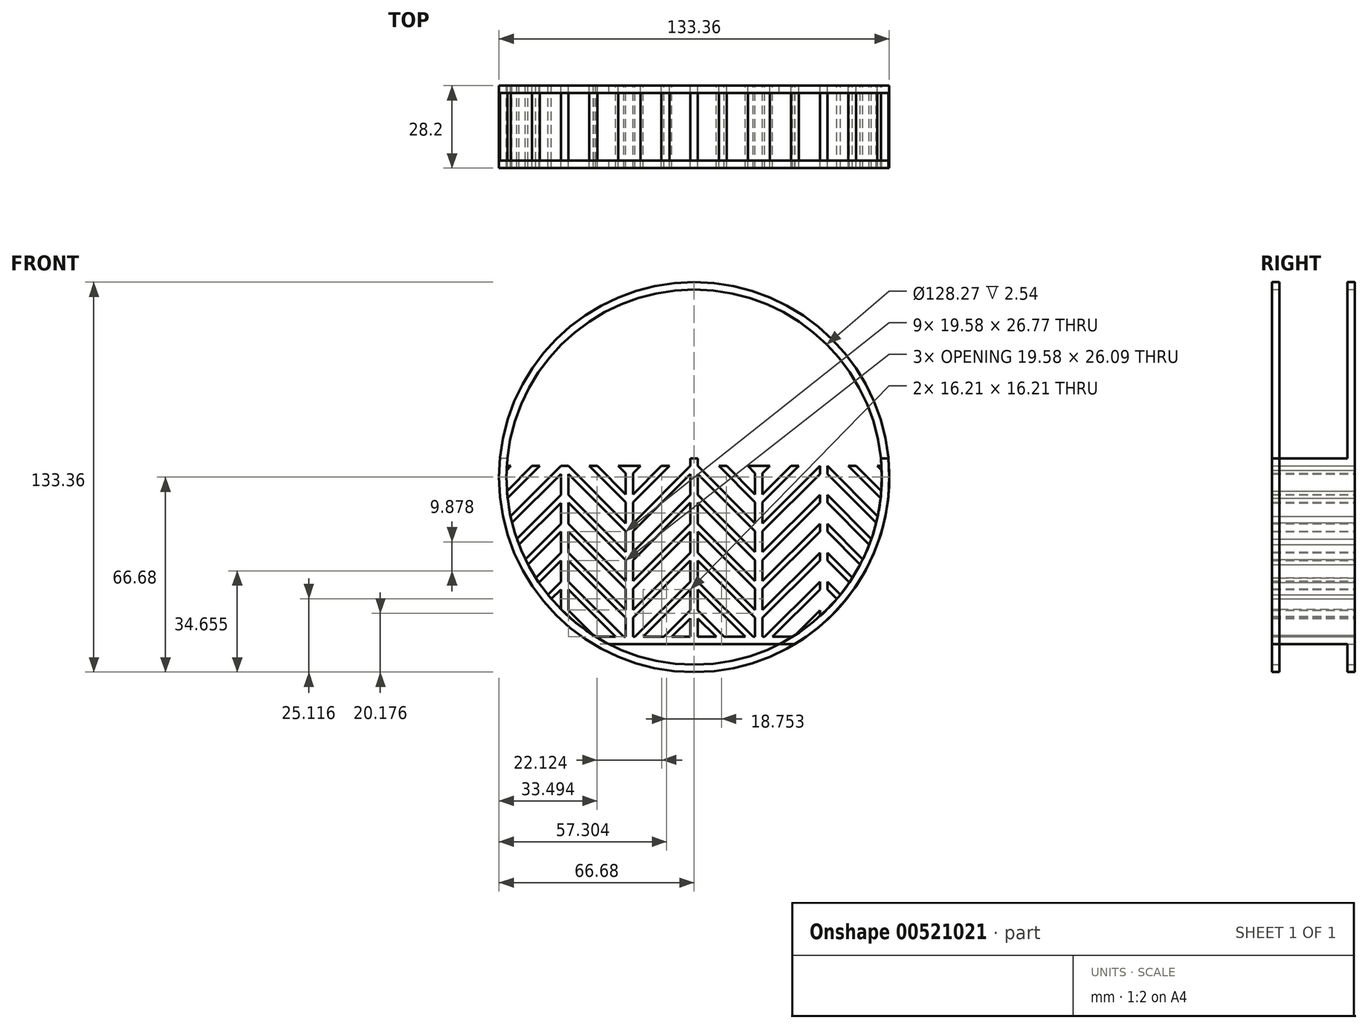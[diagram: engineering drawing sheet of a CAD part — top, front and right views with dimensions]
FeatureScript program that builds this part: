
annotation { "Feature Type Name" : "Feature", "Feature Type Description" : "" }
export const myFeature = defineFeature(function(context is Context, id is Id, definition is map)
    precondition{}
    {
        {
            var Q0;
            Q0=qCreatedBy(makeId("Front.planeOp"),FACE);
            var sketch = newSketch(context, id + "F0", { "sketchPlane" : qUnion([Q0])});
            skCircle(sketch, "E0", {"center": v(0, 0) * mm, "radius": 66.68 * mm, "construction": true});
            skLineSegment(sketch, "E1", {"start": v(-66.37, 6.35) * mm, "end": v(66.37, 6.35) * mm});
            skLineSegment(sketch, "E2", {"start": v(-34.34, -57.15) * mm, "end": v(34.34, -57.15) * mm});
            skArc(sketch, "E3", {"start": v(-66.37, 6.35) * mm, "mid": v(-59.53, -30.03) * mm, "end": v(-34.34, -57.15) * mm});
            skArc(sketch, "E4", {"start": v(66.37, 6.35) * mm, "mid": v(59.53, -30.03) * mm, "end": v(34.34, -57.15) * mm});
            skLineSegment(sketch, "E5", {"start": v(0, 6.35) * mm, "end": v(0, -57.15) * mm});
            skLineSegment(sketch, "E6", {"start": v(0, 6.35) * mm, "end": v(-22.12, 6.35) * mm});
            skLineSegment(sketch, "E7", {"start": v(-22.12, 6.35) * mm, "end": v(-44.25, 6.35) * mm});
            skLineSegment(sketch, "E8", {"start": v(-44.25, 6.35) * mm, "end": v(-66.37, 6.35) * mm});
            skLineSegment(sketch, "E9", {"start": v(0, 6.35) * mm, "end": v(22.12, 6.35) * mm});
            skLineSegment(sketch, "E10", {"start": v(22.12, 6.35) * mm, "end": v(44.25, 6.35) * mm});
            skLineSegment(sketch, "E11", {"start": v(44.25, 6.35) * mm, "end": v(66.37, 6.35) * mm});
            skLineSegment(sketch, "E12", {"start": v(-44.25, 6.35) * mm, "end": v(-44.25, -49.88) * mm, "construction": true});
            skLineSegment(sketch, "E13", {"start": v(-22.12, 6.35) * mm, "end": v(-22.12, -57.15) * mm, "construction": true});
            skLineSegment(sketch, "E14", {"start": v(22.12, 6.35) * mm, "end": v(22.12, -57.15) * mm, "construction": true});
            skLineSegment(sketch, "E15", {"start": v(44.25, 6.35) * mm, "end": v(44.25, -49.88) * mm, "construction": true});
            skCircle(sketch, "E16", {"center": v(0, 0) * mm, "radius": 64.14 * mm, "construction": true});
            skArc(sketch, "E17", {"start": v(-63.82, 6.35) * mm, "mid": v(-56.28, -30.76) * mm, "end": v(-29.1, -57.15) * mm});
            skArc(sketch, "E18", {"start": v(63.82, 6.35) * mm, "mid": v(56.28, -30.76) * mm, "end": v(29.1, -57.15) * mm});
            skLineSegment(sketch, "E19", {"start": v(-45.52, 6.35) * mm, "end": v(-45.52, -45.18) * mm});
            skLineSegment(sketch, "E20", {"start": v(-42.98, 6.35) * mm, "end": v(-42.98, -47.6) * mm});
            skLineSegment(sketch, "E21", {"start": v(-23.4, 6.35) * mm, "end": v(-23.4, -57.15) * mm});
            skLineSegment(sketch, "E22", {"start": v(-20.85, 6.35) * mm, "end": v(-20.85, -57.15) * mm});
            skLineSegment(sketch, "E23", {"start": v(-1.27, 6.35) * mm, "end": v(-1.27, -57.15) * mm});
            skLineSegment(sketch, "E24", {"start": v(1.27, 6.35) * mm, "end": v(1.27, -57.15) * mm});
            skLineSegment(sketch, "E25", {"start": v(20.85, 6.35) * mm, "end": v(20.85, -57.15) * mm});
            skLineSegment(sketch, "E26", {"start": v(23.4, 6.35) * mm, "end": v(23.4, -57.15) * mm});
            skLineSegment(sketch, "E27", {"start": v(42.98, 6.35) * mm, "end": v(42.98, -47.6) * mm});
            skLineSegment(sketch, "E28", {"start": v(45.52, 6.35) * mm, "end": v(45.52, -45.18) * mm});
            skLineSegment(sketch, "E29", {"start": v(-66.57, 3.81) * mm, "end": v(64.02, 3.81) * mm});
            skLineSegment(sketch, "E30", {"start": v(-33.63, -54.61) * mm, "end": v(33.63, -54.61) * mm});
            skLineSegment(sketch, "E31", {"start": v(-63.96, -4.75) * mm, "end": v(-55.4, 3.81) * mm});
            skLineSegment(sketch, "E32", {"start": v(-63.73, -7.22) * mm, "end": v(-52.7, 3.81) * mm});
            skLineSegment(sketch, "E33", {"start": v(-62.72, -13.4) * mm, "end": v(-45.52, 3.81) * mm});
            skLineSegment(sketch, "E34", {"start": v(-62.21, -15.58) * mm, "end": v(-45.52, 1.12) * mm});
            skLineSegment(sketch, "E35", {"start": v(-60.56, -21.11) * mm, "end": v(-45.52, -6.07) * mm});
            skLineSegment(sketch, "E36", {"start": v(-59.83, -23.1) * mm, "end": v(-45.52, -8.8) * mm});
            skLineSegment(sketch, "E37", {"start": v(-57.65, -28.1) * mm, "end": v(-45.52, -15.98) * mm});
            skLineSegment(sketch, "E38", {"start": v(-56.74, -29.9) * mm, "end": v(-45.52, -18.67) * mm});
            skLineSegment(sketch, "E39", {"start": v(-54.1, -34.44) * mm, "end": v(-45.52, -25.85) * mm});
            skLineSegment(sketch, "E40", {"start": v(-53.03, -36.06) * mm, "end": v(-45.52, -28.55) * mm});
            skLineSegment(sketch, "E41", {"start": v(-49.98, -40.2) * mm, "end": v(-45.52, -35.73) * mm});
            skLineSegment(sketch, "E42", {"start": v(-48.76, -41.67) * mm, "end": v(-45.52, -38.43) * mm});
            skLineSegment(sketch, "E43", {"start": v(-64.1, 2.3) * mm, "end": v(-62.58, 3.81) * mm});
            skLineSegment(sketch, "E44", {"start": v(-52.7, 3.81) * mm, "end": v(-52.7, 6.35) * mm, "construction": true});
            skLineSegment(sketch, "E45", {"start": v(-42.98, 3.81) * mm, "end": v(-23.4, -15.77) * mm});
            skLineSegment(sketch, "E46", {"start": v(-42.98, 1.12) * mm, "end": v(-23.4, -18.47) * mm});
            skLineSegment(sketch, "E47", {"start": v(-42.98, -6.07) * mm, "end": v(-23.4, -25.65) * mm});
            skLineSegment(sketch, "E48", {"start": v(-42.98, -8.76) * mm, "end": v(-23.4, -28.35) * mm});
            skLineSegment(sketch, "E49", {"start": v(-42.98, -15.95) * mm, "end": v(-23.4, -35.53) * mm});
            skLineSegment(sketch, "E50", {"start": v(-42.98, -18.64) * mm, "end": v(-23.4, -38.22) * mm});
            skLineSegment(sketch, "E51", {"start": v(-42.98, -25.82) * mm, "end": v(-23.4, -45.4) * mm});
            skLineSegment(sketch, "E52", {"start": v(-42.98, -28.52) * mm, "end": v(-23.4, -48.1) * mm});
            skLineSegment(sketch, "E53", {"start": v(-42.98, -35.7) * mm, "end": v(-24.07, -54.61) * mm});
            skLineSegment(sketch, "E54", {"start": v(-42.98, -45.58) * mm, "end": v(-34.48, -54.08) * mm});
            skLineSegment(sketch, "E55", {"start": v(-42.98, -38.4) * mm, "end": v(-26.77, -54.61) * mm});
            skLineSegment(sketch, "E56", {"start": v(-35.8, 3.81) * mm, "end": v(-23.4, -8.59) * mm});
            skLineSegment(sketch, "E57", {"start": v(-33.1, 3.81) * mm, "end": v(-23.4, -5.9) * mm});
            skLineSegment(sketch, "E58", {"start": v(-25.92, 3.81) * mm, "end": v(-23.4, 1.29) * mm});
            skLineSegment(sketch, "E59", {"start": v(-1.27, 3.81) * mm, "end": v(-20.85, -15.77) * mm});
            skLineSegment(sketch, "E60", {"start": v(-8.45, 3.81) * mm, "end": v(-20.85, -8.59) * mm});
            skLineSegment(sketch, "E61", {"start": v(-11.15, 3.81) * mm, "end": v(-20.85, -5.9) * mm});
            skLineSegment(sketch, "E62", {"start": v(-18.33, 3.81) * mm, "end": v(-20.85, 1.29) * mm});
            skLineSegment(sketch, "E63", {"start": v(-1.27, 1.12) * mm, "end": v(-20.85, -18.47) * mm});
            skLineSegment(sketch, "E64", {"start": v(-20.85, -25.65) * mm, "end": v(-1.27, -6.07) * mm});
            skLineSegment(sketch, "E65", {"start": v(-20.85, -28.35) * mm, "end": v(-1.27, -8.76) * mm});
            skLineSegment(sketch, "E66", {"start": v(-20.85, -35.53) * mm, "end": v(-1.27, -15.95) * mm});
            skLineSegment(sketch, "E67", {"start": v(-20.85, -38.22) * mm, "end": v(-1.27, -18.64) * mm});
            skLineSegment(sketch, "E68", {"start": v(-20.85, -45.4) * mm, "end": v(-1.27, -25.82) * mm});
            skLineSegment(sketch, "E69", {"start": v(-20.85, -48.1) * mm, "end": v(-1.27, -28.52) * mm});
            skLineSegment(sketch, "E70", {"start": v(-20.18, -54.61) * mm, "end": v(-1.27, -35.7) * mm});
            skLineSegment(sketch, "E71", {"start": v(-17.48, -54.61) * mm, "end": v(-1.27, -38.4) * mm});
            skLineSegment(sketch, "E72", {"start": v(-10.3, -54.61) * mm, "end": v(-1.27, -45.58) * mm});
            skLineSegment(sketch, "E73", {"start": v(-7.6, -54.61) * mm, "end": v(-1.27, -48.28) * mm});
            skLineSegment(sketch, "E74", {"start": v(1.27, 3.81) * mm, "end": v(20.85, -15.77) * mm});
            skLineSegment(sketch, "E75", {"start": v(1.27, 1.12) * mm, "end": v(20.85, -18.47) * mm});
            skLineSegment(sketch, "E76", {"start": v(1.27, -6.07) * mm, "end": v(20.85, -25.65) * mm});
            skLineSegment(sketch, "E77", {"start": v(1.27, -8.76) * mm, "end": v(20.85, -28.35) * mm});
            skLineSegment(sketch, "E78", {"start": v(1.27, -15.95) * mm, "end": v(20.85, -35.53) * mm});
            skLineSegment(sketch, "E79", {"start": v(1.27, -18.64) * mm, "end": v(20.85, -38.22) * mm});
            skLineSegment(sketch, "E80", {"start": v(1.27, -25.82) * mm, "end": v(20.85, -45.4) * mm});
            skLineSegment(sketch, "E81", {"start": v(1.27, -28.52) * mm, "end": v(20.85, -48.1) * mm});
            skLineSegment(sketch, "E82", {"start": v(1.27, -35.7) * mm, "end": v(20.18, -54.61) * mm});
            skLineSegment(sketch, "E83", {"start": v(1.27, -38.4) * mm, "end": v(17.48, -54.61) * mm});
            skLineSegment(sketch, "E84", {"start": v(1.27, -45.58) * mm, "end": v(10.3, -54.61) * mm});
            skLineSegment(sketch, "E85", {"start": v(1.27, -48.28) * mm, "end": v(7.6, -54.61) * mm});
            skLineSegment(sketch, "E86", {"start": v(8.45, 3.81) * mm, "end": v(20.85, -8.59) * mm});
            skLineSegment(sketch, "E87", {"start": v(11.15, 3.81) * mm, "end": v(20.85, -5.9) * mm});
            skLineSegment(sketch, "E88", {"start": v(18.33, 3.81) * mm, "end": v(20.85, 1.29) * mm});
            skLineSegment(sketch, "E89", {"start": v(23.4, -5.9) * mm, "end": v(33.1, 3.81) * mm});
            skLineSegment(sketch, "E90", {"start": v(23.4, 1.29) * mm, "end": v(25.92, 3.81) * mm});
            skLineSegment(sketch, "E91", {"start": v(23.4, -15.77) * mm, "end": v(42.98, 3.81) * mm});
            skLineSegment(sketch, "E92", {"start": v(23.4, -8.59) * mm, "end": v(35.8, 3.81) * mm});
            skLineSegment(sketch, "E93", {"start": v(23.4, -18.47) * mm, "end": v(42.98, 1.12) * mm});
            skLineSegment(sketch, "E94", {"start": v(23.4, -25.65) * mm, "end": v(42.98, -6.07) * mm});
            skLineSegment(sketch, "E95", {"start": v(23.4, -28.35) * mm, "end": v(42.98, -8.76) * mm});
            skLineSegment(sketch, "E96", {"start": v(23.4, -35.53) * mm, "end": v(42.98, -15.95) * mm});
            skLineSegment(sketch, "E97", {"start": v(23.4, -38.22) * mm, "end": v(42.98, -18.64) * mm});
            skLineSegment(sketch, "E98", {"start": v(23.4, -45.4) * mm, "end": v(42.98, -25.82) * mm});
            skLineSegment(sketch, "E99", {"start": v(23.4, -48.1) * mm, "end": v(42.98, -28.52) * mm});
            skLineSegment(sketch, "E100", {"start": v(24.07, -54.61) * mm, "end": v(42.98, -35.7) * mm});
            skLineSegment(sketch, "E101", {"start": v(26.77, -54.61) * mm, "end": v(42.98, -38.4) * mm});
            skLineSegment(sketch, "E102", {"start": v(42.98, -45.58) * mm, "end": v(34.48, -54.08) * mm});
            skLineSegment(sketch, "E103", {"start": v(45.52, 3.81) * mm, "end": v(62.72, -13.4) * mm});
            skLineSegment(sketch, "E104", {"start": v(45.52, 1.12) * mm, "end": v(62.21, -15.58) * mm});
            skLineSegment(sketch, "E105", {"start": v(45.52, -6.07) * mm, "end": v(60.56, -21.11) * mm});
            skLineSegment(sketch, "E106", {"start": v(45.52, -8.76) * mm, "end": v(59.84, -23.08) * mm});
            skLineSegment(sketch, "E107", {"start": v(45.52, -15.95) * mm, "end": v(57.66, -28.09) * mm});
            skLineSegment(sketch, "E108", {"start": v(45.52, -18.64) * mm, "end": v(56.75, -29.87) * mm});
            skLineSegment(sketch, "E109", {"start": v(45.52, -25.82) * mm, "end": v(54.11, -34.42) * mm});
            skLineSegment(sketch, "E110", {"start": v(45.52, -28.52) * mm, "end": v(53.05, -36.05) * mm});
            skLineSegment(sketch, "E111", {"start": v(45.52, -35.7) * mm, "end": v(50, -40.18) * mm});
            skLineSegment(sketch, "E112", {"start": v(45.52, -38.4) * mm, "end": v(48.77, -41.65) * mm});
            skLineSegment(sketch, "E113", {"start": v(52.7, 3.81) * mm, "end": v(63.73, -7.22) * mm});
            skLineSegment(sketch, "E114", {"start": v(55.4, 3.81) * mm, "end": v(63.96, -4.75) * mm});
            skLineSegment(sketch, "E115", {"start": v(62.58, 3.81) * mm, "end": v(64.1, 2.3) * mm});
            skSolve(sketch);
        }
        {
            var Q0;
            Q0=qCreatedBy(makeId("Front.planeOp"),FACE);
            var sketch = newSketch(context, id + "F1", { "sketchPlane" : qUnion([Q0])});
            skCircle(sketch, "E116", {"center": v(0, 0) * mm, "radius": 66.68 * mm});
            skCircle(sketch, "E117", {"center": v(0, 0) * mm, "radius": 64.14 * mm});
            skSolve(sketch);
        }
        {
            var Q0;
            Q0=makeQuery(id+"F1.imprint","IMPRINT",FACE,{"disambiguationData":[TD([[makeQuery(id+"F1.imprint","IMPRINT",EDGE,{"derivedFrom":sQuery(id+"F1.wireOp",EDGE,"E116")}),1.0]])]});
            extrude(context, id + "F2", {"entities" : qUnion([Q0]), "depth" : 2.54 * mm, "offsetDistance" : 25.4 * mm});
        }
        {
            var Q0;
            {var subQ0=sQuery(id+"F0.wireOp",EDGE,"E26");var subQ1=sQuery(id+"F0.wireOp",EDGE,"E10");var subQ2=makeQuery(id+"F0.imprint","INTERSECT",VERTEX,{"derivedFrom":[subQ1,subQ0]});Q0=makeQuery(id+"F0.imprint","IMPRINT",FACE,{"disambiguationData":[TD([[makeQuery(id+"F0.imprint","IMPRINT",EDGE,{"disambiguationData":[TD([[subQ2,-1.0]])],"derivedFrom":subQ1}),-1.0]])]});}
            var Q1;
            {var subQ4=sQuery(id+"F0.wireOp",EDGE,"E18");var subQ5=sQuery(id+"F0.wireOp",EDGE,"E11");var subQ6=makeQuery(id+"F0.imprint","INTERSECT",VERTEX,{"derivedFrom":[subQ5,subQ4]});Q1=makeQuery(id+"F0.imprint","IMPRINT",FACE,{"disambiguationData":[TD([[makeQuery(id+"F0.imprint","IMPRINT",EDGE,{"disambiguationData":[TD([[subQ6,1.0]])],"derivedFrom":subQ5}),-1.0]])]});}
            var Q2;
            {var subQ1=sQuery(id+"F0.wireOp",EDGE,"E24");var subQ4=sQuery(id+"F0.wireOp",EDGE,"E9");var subQ5=makeQuery(id+"F0.imprint","INTERSECT",VERTEX,{"derivedFrom":[subQ4,subQ1]});Q2=makeQuery(id+"F0.imprint","IMPRINT",FACE,{"disambiguationData":[TD([[makeQuery(id+"F0.imprint","IMPRINT",EDGE,{"disambiguationData":[TD([[subQ5,-1.0]])],"derivedFrom":subQ4}),-1.0]])]});}
            var Q3;
            {var subQ2=sQuery(id+"F0.wireOp",EDGE,"E22");var subQ5=sQuery(id+"F0.wireOp",EDGE,"E6");var subQ8=makeQuery(id+"F0.imprint","INTERSECT",VERTEX,{"derivedFrom":[subQ5,subQ2]});Q3=makeQuery(id+"F0.imprint","IMPRINT",FACE,{"disambiguationData":[TD([[makeQuery(id+"F0.imprint","IMPRINT",EDGE,{"disambiguationData":[TD([[subQ8,1.0]])],"derivedFrom":subQ5}),1.0]])]});}
            var Q4;
            {var subQ1=sQuery(id+"F0.wireOp",EDGE,"E20");var subQ4=sQuery(id+"F0.wireOp",EDGE,"E7");var subQ5=makeQuery(id+"F0.imprint","INTERSECT",VERTEX,{"derivedFrom":[subQ4,subQ1]});Q4=makeQuery(id+"F0.imprint","IMPRINT",FACE,{"disambiguationData":[TD([[makeQuery(id+"F0.imprint","IMPRINT",EDGE,{"disambiguationData":[TD([[subQ5,1.0]])],"derivedFrom":subQ4}),1.0]])]});}
            var Q5;
            {var subQ1=sQuery(id+"F0.wireOp",EDGE,"E8");var subQ7=sQuery(id+"F0.wireOp",EDGE,"E17");var subQ8=makeQuery(id+"F0.imprint","INTERSECT",VERTEX,{"derivedFrom":[subQ1,subQ7]});Q5=makeQuery(id+"F0.imprint","IMPRINT",FACE,{"disambiguationData":[TD([[makeQuery(id+"F0.imprint","IMPRINT",EDGE,{"disambiguationData":[TD([[subQ8,1.0]])],"derivedFrom":subQ1}),1.0]])]});}
            var Q6;
            {var subQ1=sQuery(id+"F0.wireOp",EDGE,"E7");var subQ6=sQuery(id+"F0.wireOp",EDGE,"E8");var subQ9=makeQuery(id+"F0.imprint","INTERSECT",VERTEX,{"derivedFrom":[subQ1,subQ6]});Q6=makeQuery(id+"F0.imprint","IMPRINT",FACE,{"disambiguationData":[TD([[makeQuery(id+"F0.imprint","IMPRINT",EDGE,{"disambiguationData":[TD([[subQ9,1.0]])],"derivedFrom":subQ1}),1.0]])]});}
            var Q7;
            {var subQ1=sQuery(id+"F0.wireOp",EDGE,"E17");var subQ15=sQuery(id+"F0.wireOp",EDGE,"E19");var subQ16=makeQuery(id+"F0.imprint","INTERSECT",VERTEX,{"derivedFrom":[subQ1,subQ15]});Q7=makeQuery(id+"F0.imprint","IMPRINT",FACE,{"disambiguationData":[TD([[makeQuery(id+"F0.imprint","IMPRINT",EDGE,{"disambiguationData":[TD([[subQ16,-1.0]])],"derivedFrom":subQ1}),1.0]])]});}
            var Q8;
            {var subQ1=sQuery(id+"F0.wireOp",EDGE,"E7");var subQ5=sQuery(id+"F0.wireOp",EDGE,"E6");var subQ6=makeQuery(id+"F0.imprint","INTERSECT",VERTEX,{"derivedFrom":[subQ5,subQ1]});Q8=makeQuery(id+"F0.imprint","IMPRINT",FACE,{"disambiguationData":[TD([[makeQuery(id+"F0.imprint","IMPRINT",EDGE,{"disambiguationData":[TD([[subQ6,1.0]])],"derivedFrom":subQ5}),1.0]])]});}
            var Q9;
            {var subQ4=sQuery(id+"F0.wireOp",EDGE,"E21");var subQ21=makeQuery(id+"F0.imprint","INTERSECT",VERTEX,{"derivedFrom":[subQ4,sQuery(id+"F0.wireOp",EDGE,"E58")]});Q9=makeQuery(id+"F0.imprint","IMPRINT",FACE,{"disambiguationData":[TD([[makeQuery(id+"F0.imprint","IMPRINT",EDGE,{"disambiguationData":[TD([[subQ21,1.0]])],"derivedFrom":subQ4}),1.0]])]});}
            var Q10;
            {var subQ1=sQuery(id+"F0.wireOp",EDGE,"E5");var subQ3=sQuery(id+"F0.wireOp",EDGE,"E29");var subQ4=makeQuery(id+"F0.imprint","INTERSECT",VERTEX,{"derivedFrom":[subQ1,subQ3]});Q10=makeQuery(id+"F0.imprint","IMPRINT",FACE,{"disambiguationData":[TD([[makeQuery(id+"F0.imprint","IMPRINT",EDGE,{"disambiguationData":[TD([[subQ4,1.0]])],"derivedFrom":subQ1}),-1.0]])]});}
            var Q11;
            {var subQ6=sQuery(id+"F0.wireOp",EDGE,"E29");var subQ7=sQuery(id+"F0.wireOp",EDGE,"E5");var subQ8=makeQuery(id+"F0.imprint","INTERSECT",VERTEX,{"derivedFrom":[subQ7,subQ6]});Q11=makeQuery(id+"F0.imprint","IMPRINT",FACE,{"disambiguationData":[TD([[makeQuery(id+"F0.imprint","IMPRINT",EDGE,{"disambiguationData":[TD([[subQ8,-1.0]])],"derivedFrom":subQ7}),-1.0]])]});}
            var Q12;
            {var subQ1=sQuery(id+"F0.wireOp",EDGE,"E5");var subQ3=sQuery(id+"F0.wireOp",EDGE,"E29");var subQ4=makeQuery(id+"F0.imprint","INTERSECT",VERTEX,{"derivedFrom":[subQ1,subQ3]});Q12=makeQuery(id+"F0.imprint","IMPRINT",FACE,{"disambiguationData":[TD([[makeQuery(id+"F0.imprint","IMPRINT",EDGE,{"disambiguationData":[TD([[subQ4,1.0]])],"derivedFrom":subQ1}),1.0]])]});}
            var Q13;
            {var subQ8=sQuery(id+"F0.wireOp",EDGE,"E29");var subQ9=sQuery(id+"F0.wireOp",EDGE,"E5");var subQ10=makeQuery(id+"F0.imprint","INTERSECT",VERTEX,{"derivedFrom":[subQ9,subQ8]});Q13=makeQuery(id+"F0.imprint","IMPRINT",FACE,{"disambiguationData":[TD([[makeQuery(id+"F0.imprint","IMPRINT",EDGE,{"disambiguationData":[TD([[subQ10,-1.0]])],"derivedFrom":subQ9}),1.0]])]});}
            var Q14;
            {var subQ1=sQuery(id+"F0.wireOp",EDGE,"E10");var subQ6=sQuery(id+"F0.wireOp",EDGE,"E9");var subQ9=makeQuery(id+"F0.imprint","INTERSECT",VERTEX,{"derivedFrom":[subQ6,subQ1]});Q14=makeQuery(id+"F0.imprint","IMPRINT",FACE,{"disambiguationData":[TD([[makeQuery(id+"F0.imprint","IMPRINT",EDGE,{"disambiguationData":[TD([[subQ9,1.0]])],"derivedFrom":subQ6}),-1.0]])]});}
            var Q15;
            {var subQ12=sQuery(id+"F0.wireOp",EDGE,"E25");var subQ21=makeQuery(id+"F0.imprint","INTERSECT",VERTEX,{"derivedFrom":[subQ12,sQuery(id+"F0.wireOp",EDGE,"E88")]});Q15=makeQuery(id+"F0.imprint","IMPRINT",FACE,{"disambiguationData":[TD([[makeQuery(id+"F0.imprint","IMPRINT",EDGE,{"disambiguationData":[TD([[subQ21,1.0]])],"derivedFrom":subQ12}),1.0]])]});}
            var Q16;
            {var subQ1=sQuery(id+"F0.wireOp",EDGE,"E10");var subQ6=sQuery(id+"F0.wireOp",EDGE,"E11");var subQ9=makeQuery(id+"F0.imprint","INTERSECT",VERTEX,{"derivedFrom":[subQ1,subQ6]});Q16=makeQuery(id+"F0.imprint","IMPRINT",FACE,{"disambiguationData":[TD([[makeQuery(id+"F0.imprint","IMPRINT",EDGE,{"disambiguationData":[TD([[subQ9,1.0]])],"derivedFrom":subQ1}),-1.0]])]});}
            var Q17;
            {var subQ1=sQuery(id+"F0.wireOp",EDGE,"E18");var subQ14=sQuery(id+"F0.wireOp",EDGE,"E27");var subQ15=makeQuery(id+"F0.imprint","INTERSECT",VERTEX,{"derivedFrom":[subQ1,subQ14]});Q17=makeQuery(id+"F0.imprint","IMPRINT",FACE,{"disambiguationData":[TD([[makeQuery(id+"F0.imprint","IMPRINT",EDGE,{"disambiguationData":[TD([[subQ15,1.0]])],"derivedFrom":subQ1}),-1.0]])]});}
            var Q18;
            {var subQ3=sQuery(id+"F0.wireOp",EDGE,"E115");Q18=makeQuery(id+"F0.imprint","IMPRINT",FACE,{"disambiguationData":[TD([[makeQuery(id+"F0.imprint","IMPRINT",EDGE,{"derivedFrom":subQ3}),1.0]])]});}
            var Q19;
            {var subQ0=sQuery(id+"F0.wireOp",EDGE,"E113");Q19=makeQuery(id+"F0.imprint","IMPRINT",FACE,{"disambiguationData":[TD([[makeQuery(id+"F0.imprint","IMPRINT",EDGE,{"derivedFrom":subQ0}),1.0]])]});}
            var Q20;
            {var subQ0=sQuery(id+"F0.wireOp",EDGE,"E103");Q20=makeQuery(id+"F0.imprint","IMPRINT",FACE,{"disambiguationData":[TD([[makeQuery(id+"F0.imprint","IMPRINT",EDGE,{"derivedFrom":subQ0}),-1.0]])]});}
            var Q21;
            {var subQ0=sQuery(id+"F0.wireOp",EDGE,"E105");Q21=makeQuery(id+"F0.imprint","IMPRINT",FACE,{"disambiguationData":[TD([[makeQuery(id+"F0.imprint","IMPRINT",EDGE,{"derivedFrom":subQ0}),-1.0]])]});}
            var Q22;
            {var subQ0=sQuery(id+"F0.wireOp",EDGE,"E107");Q22=makeQuery(id+"F0.imprint","IMPRINT",FACE,{"disambiguationData":[TD([[makeQuery(id+"F0.imprint","IMPRINT",EDGE,{"derivedFrom":subQ0}),-1.0]])]});}
            var Q23;
            {var subQ0=sQuery(id+"F0.wireOp",EDGE,"E109");Q23=makeQuery(id+"F0.imprint","IMPRINT",FACE,{"disambiguationData":[TD([[makeQuery(id+"F0.imprint","IMPRINT",EDGE,{"derivedFrom":subQ0}),-1.0]])]});}
            var Q24;
            {var subQ0=sQuery(id+"F0.wireOp",EDGE,"E111");Q24=makeQuery(id+"F0.imprint","IMPRINT",FACE,{"disambiguationData":[TD([[makeQuery(id+"F0.imprint","IMPRINT",EDGE,{"derivedFrom":subQ0}),-1.0]])]});}
            var Q25;
            {var subQ3=sQuery(id+"F0.wireOp",EDGE,"E102");Q25=makeQuery(id+"F0.imprint","IMPRINT",FACE,{"disambiguationData":[TD([[makeQuery(id+"F0.imprint","IMPRINT",EDGE,{"derivedFrom":subQ3}),1.0]])]});}
            var Q26;
            {var subQ0=sQuery(id+"F0.wireOp",EDGE,"E100");Q26=makeQuery(id+"F0.imprint","IMPRINT",FACE,{"disambiguationData":[TD([[makeQuery(id+"F0.imprint","IMPRINT",EDGE,{"derivedFrom":subQ0}),-1.0]])]});}
            var Q27;
            {var subQ0=sQuery(id+"F0.wireOp",EDGE,"E98");Q27=makeQuery(id+"F0.imprint","IMPRINT",FACE,{"disambiguationData":[TD([[makeQuery(id+"F0.imprint","IMPRINT",EDGE,{"derivedFrom":subQ0}),-1.0]])]});}
            var Q28;
            {var subQ0=sQuery(id+"F0.wireOp",EDGE,"E96");Q28=makeQuery(id+"F0.imprint","IMPRINT",FACE,{"disambiguationData":[TD([[makeQuery(id+"F0.imprint","IMPRINT",EDGE,{"derivedFrom":subQ0}),-1.0]])]});}
            var Q29;
            {var subQ0=sQuery(id+"F0.wireOp",EDGE,"E94");Q29=makeQuery(id+"F0.imprint","IMPRINT",FACE,{"disambiguationData":[TD([[makeQuery(id+"F0.imprint","IMPRINT",EDGE,{"derivedFrom":subQ0}),-1.0]])]});}
            var Q30;
            {var subQ0=sQuery(id+"F0.wireOp",EDGE,"E91");Q30=makeQuery(id+"F0.imprint","IMPRINT",FACE,{"disambiguationData":[TD([[makeQuery(id+"F0.imprint","IMPRINT",EDGE,{"derivedFrom":subQ0}),-1.0]])]});}
            var Q31;
            {var subQ0=sQuery(id+"F0.wireOp",EDGE,"E89");Q31=makeQuery(id+"F0.imprint","IMPRINT",FACE,{"disambiguationData":[TD([[makeQuery(id+"F0.imprint","IMPRINT",EDGE,{"derivedFrom":subQ0}),-1.0]])]});}
            var Q32;
            {var subQ0=sQuery(id+"F0.wireOp",EDGE,"E90");Q32=makeQuery(id+"F0.imprint","IMPRINT",FACE,{"disambiguationData":[TD([[makeQuery(id+"F0.imprint","IMPRINT",EDGE,{"derivedFrom":subQ0}),1.0]])]});}
            var Q33;
            {var subQ0=sQuery(id+"F0.wireOp",EDGE,"E88");Q33=makeQuery(id+"F0.imprint","IMPRINT",FACE,{"disambiguationData":[TD([[makeQuery(id+"F0.imprint","IMPRINT",EDGE,{"derivedFrom":subQ0}),1.0]])]});}
            var Q34;
            {var subQ0=sQuery(id+"F0.wireOp",EDGE,"E86");Q34=makeQuery(id+"F0.imprint","IMPRINT",FACE,{"disambiguationData":[TD([[makeQuery(id+"F0.imprint","IMPRINT",EDGE,{"derivedFrom":subQ0}),1.0]])]});}
            var Q35;
            {var subQ0=sQuery(id+"F0.wireOp",EDGE,"E74");Q35=makeQuery(id+"F0.imprint","IMPRINT",FACE,{"disambiguationData":[TD([[makeQuery(id+"F0.imprint","IMPRINT",EDGE,{"derivedFrom":subQ0}),-1.0]])]});}
            var Q36;
            {var subQ0=sQuery(id+"F0.wireOp",EDGE,"E76");Q36=makeQuery(id+"F0.imprint","IMPRINT",FACE,{"disambiguationData":[TD([[makeQuery(id+"F0.imprint","IMPRINT",EDGE,{"derivedFrom":subQ0}),-1.0]])]});}
            var Q37;
            {var subQ0=sQuery(id+"F0.wireOp",EDGE,"E78");Q37=makeQuery(id+"F0.imprint","IMPRINT",FACE,{"disambiguationData":[TD([[makeQuery(id+"F0.imprint","IMPRINT",EDGE,{"derivedFrom":subQ0}),-1.0]])]});}
            var Q38;
            {var subQ0=sQuery(id+"F0.wireOp",EDGE,"E80");Q38=makeQuery(id+"F0.imprint","IMPRINT",FACE,{"disambiguationData":[TD([[makeQuery(id+"F0.imprint","IMPRINT",EDGE,{"derivedFrom":subQ0}),-1.0]])]});}
            var Q39;
            {var subQ0=sQuery(id+"F0.wireOp",EDGE,"E82");Q39=makeQuery(id+"F0.imprint","IMPRINT",FACE,{"disambiguationData":[TD([[makeQuery(id+"F0.imprint","IMPRINT",EDGE,{"derivedFrom":subQ0}),-1.0]])]});}
            var Q40;
            {var subQ0=sQuery(id+"F0.wireOp",EDGE,"E84");Q40=makeQuery(id+"F0.imprint","IMPRINT",FACE,{"disambiguationData":[TD([[makeQuery(id+"F0.imprint","IMPRINT",EDGE,{"derivedFrom":subQ0}),-1.0]])]});}
            var Q41;
            {var subQ0=sQuery(id+"F0.wireOp",EDGE,"E72");Q41=makeQuery(id+"F0.imprint","IMPRINT",FACE,{"disambiguationData":[TD([[makeQuery(id+"F0.imprint","IMPRINT",EDGE,{"derivedFrom":subQ0}),-1.0]])]});}
            var Q42;
            {var subQ0=sQuery(id+"F0.wireOp",EDGE,"E70");Q42=makeQuery(id+"F0.imprint","IMPRINT",FACE,{"disambiguationData":[TD([[makeQuery(id+"F0.imprint","IMPRINT",EDGE,{"derivedFrom":subQ0}),-1.0]])]});}
            var Q43;
            {var subQ0=sQuery(id+"F0.wireOp",EDGE,"E68");Q43=makeQuery(id+"F0.imprint","IMPRINT",FACE,{"disambiguationData":[TD([[makeQuery(id+"F0.imprint","IMPRINT",EDGE,{"derivedFrom":subQ0}),-1.0]])]});}
            var Q44;
            {var subQ0=sQuery(id+"F0.wireOp",EDGE,"E66");Q44=makeQuery(id+"F0.imprint","IMPRINT",FACE,{"disambiguationData":[TD([[makeQuery(id+"F0.imprint","IMPRINT",EDGE,{"derivedFrom":subQ0}),-1.0]])]});}
            var Q45;
            {var subQ0=sQuery(id+"F0.wireOp",EDGE,"E64");Q45=makeQuery(id+"F0.imprint","IMPRINT",FACE,{"disambiguationData":[TD([[makeQuery(id+"F0.imprint","IMPRINT",EDGE,{"derivedFrom":subQ0}),-1.0]])]});}
            var Q46;
            {var subQ0=sQuery(id+"F0.wireOp",EDGE,"E59");Q46=makeQuery(id+"F0.imprint","IMPRINT",FACE,{"disambiguationData":[TD([[makeQuery(id+"F0.imprint","IMPRINT",EDGE,{"derivedFrom":subQ0}),1.0]])]});}
            var Q47;
            {var subQ0=sQuery(id+"F0.wireOp",EDGE,"E60");Q47=makeQuery(id+"F0.imprint","IMPRINT",FACE,{"disambiguationData":[TD([[makeQuery(id+"F0.imprint","IMPRINT",EDGE,{"derivedFrom":subQ0}),-1.0]])]});}
            var Q48;
            {var subQ0=sQuery(id+"F0.wireOp",EDGE,"E62");Q48=makeQuery(id+"F0.imprint","IMPRINT",FACE,{"disambiguationData":[TD([[makeQuery(id+"F0.imprint","IMPRINT",EDGE,{"derivedFrom":subQ0}),-1.0]])]});}
            var Q49;
            {var subQ0=sQuery(id+"F0.wireOp",EDGE,"E58");Q49=makeQuery(id+"F0.imprint","IMPRINT",FACE,{"disambiguationData":[TD([[makeQuery(id+"F0.imprint","IMPRINT",EDGE,{"derivedFrom":subQ0}),1.0]])]});}
            var Q50;
            {var subQ0=sQuery(id+"F0.wireOp",EDGE,"E56");Q50=makeQuery(id+"F0.imprint","IMPRINT",FACE,{"disambiguationData":[TD([[makeQuery(id+"F0.imprint","IMPRINT",EDGE,{"derivedFrom":subQ0}),1.0]])]});}
            var Q51;
            {var subQ0=sQuery(id+"F0.wireOp",EDGE,"E45");Q51=makeQuery(id+"F0.imprint","IMPRINT",FACE,{"disambiguationData":[TD([[makeQuery(id+"F0.imprint","IMPRINT",EDGE,{"derivedFrom":subQ0}),-1.0]])]});}
            var Q52;
            {var subQ0=sQuery(id+"F0.wireOp",EDGE,"E47");Q52=makeQuery(id+"F0.imprint","IMPRINT",FACE,{"disambiguationData":[TD([[makeQuery(id+"F0.imprint","IMPRINT",EDGE,{"derivedFrom":subQ0}),-1.0]])]});}
            var Q53;
            {var subQ0=sQuery(id+"F0.wireOp",EDGE,"E49");Q53=makeQuery(id+"F0.imprint","IMPRINT",FACE,{"disambiguationData":[TD([[makeQuery(id+"F0.imprint","IMPRINT",EDGE,{"derivedFrom":subQ0}),-1.0]])]});}
            var Q54;
            {var subQ0=sQuery(id+"F0.wireOp",EDGE,"E51");Q54=makeQuery(id+"F0.imprint","IMPRINT",FACE,{"disambiguationData":[TD([[makeQuery(id+"F0.imprint","IMPRINT",EDGE,{"derivedFrom":subQ0}),-1.0]])]});}
            var Q55;
            {var subQ0=sQuery(id+"F0.wireOp",EDGE,"E53");Q55=makeQuery(id+"F0.imprint","IMPRINT",FACE,{"disambiguationData":[TD([[makeQuery(id+"F0.imprint","IMPRINT",EDGE,{"derivedFrom":subQ0}),-1.0]])]});}
            var Q56;
            {var subQ3=sQuery(id+"F0.wireOp",EDGE,"E54");Q56=makeQuery(id+"F0.imprint","IMPRINT",FACE,{"disambiguationData":[TD([[makeQuery(id+"F0.imprint","IMPRINT",EDGE,{"derivedFrom":subQ3}),-1.0]])]});}
            var Q57;
            {var subQ0=sQuery(id+"F0.wireOp",EDGE,"E41");Q57=makeQuery(id+"F0.imprint","IMPRINT",FACE,{"disambiguationData":[TD([[makeQuery(id+"F0.imprint","IMPRINT",EDGE,{"derivedFrom":subQ0}),-1.0]])]});}
            var Q58;
            {var subQ0=sQuery(id+"F0.wireOp",EDGE,"E39");Q58=makeQuery(id+"F0.imprint","IMPRINT",FACE,{"disambiguationData":[TD([[makeQuery(id+"F0.imprint","IMPRINT",EDGE,{"derivedFrom":subQ0}),-1.0]])]});}
            var Q59;
            {var subQ0=sQuery(id+"F0.wireOp",EDGE,"E37");Q59=makeQuery(id+"F0.imprint","IMPRINT",FACE,{"disambiguationData":[TD([[makeQuery(id+"F0.imprint","IMPRINT",EDGE,{"derivedFrom":subQ0}),-1.0]])]});}
            var Q60;
            {var subQ0=sQuery(id+"F0.wireOp",EDGE,"E35");Q60=makeQuery(id+"F0.imprint","IMPRINT",FACE,{"disambiguationData":[TD([[makeQuery(id+"F0.imprint","IMPRINT",EDGE,{"derivedFrom":subQ0}),-1.0]])]});}
            var Q61;
            {var subQ0=sQuery(id+"F0.wireOp",EDGE,"E33");Q61=makeQuery(id+"F0.imprint","IMPRINT",FACE,{"disambiguationData":[TD([[makeQuery(id+"F0.imprint","IMPRINT",EDGE,{"derivedFrom":subQ0}),-1.0]])]});}
            var Q62;
            {var subQ0=sQuery(id+"F0.wireOp",EDGE,"E31");Q62=makeQuery(id+"F0.imprint","IMPRINT",FACE,{"disambiguationData":[TD([[makeQuery(id+"F0.imprint","IMPRINT",EDGE,{"derivedFrom":subQ0}),-1.0]])]});}
            var Q63;
            {var subQ0=sQuery(id+"F0.wireOp",EDGE,"E43");Q63=makeQuery(id+"F0.imprint","IMPRINT",FACE,{"disambiguationData":[TD([[makeQuery(id+"F0.imprint","IMPRINT",EDGE,{"derivedFrom":subQ0}),1.0]])]});}
            var Q64;
            {var subQ1=sQuery(id+"F0.wireOp",EDGE,"E17");var subQ5=sQuery(id+"F0.wireOp",EDGE,"E2");var subQ8=makeQuery(id+"F0.imprint","INTERSECT",VERTEX,{"derivedFrom":[subQ5,subQ1]});Q64=makeQuery(id+"F0.imprint","IMPRINT",FACE,{"disambiguationData":[TD([[makeQuery(id+"F0.imprint","IMPRINT",EDGE,{"disambiguationData":[TD([[subQ8,-1.0]])],"derivedFrom":subQ5}),1.0]])]});}
            var Q65;
            {var subQ0=sQuery(id+"F0.wireOp",EDGE,"E21");var subQ1=sQuery(id+"F0.wireOp",EDGE,"E2");var subQ2=makeQuery(id+"F0.imprint","INTERSECT",VERTEX,{"derivedFrom":[subQ1,subQ0]});Q65=makeQuery(id+"F0.imprint","IMPRINT",FACE,{"disambiguationData":[TD([[makeQuery(id+"F0.imprint","IMPRINT",EDGE,{"disambiguationData":[TD([[subQ2,-1.0]])],"derivedFrom":subQ1}),1.0]])]});}
            var Q66;
            {var subQ1=sQuery(id+"F0.wireOp",EDGE,"E2");var subQ6=sQuery(id+"F0.wireOp",EDGE,"E22");var subQ8=makeQuery(id+"F0.imprint","INTERSECT",VERTEX,{"derivedFrom":[subQ1,subQ6]});Q66=makeQuery(id+"F0.imprint","IMPRINT",FACE,{"disambiguationData":[TD([[makeQuery(id+"F0.imprint","IMPRINT",EDGE,{"disambiguationData":[TD([[subQ8,-1.0]])],"derivedFrom":subQ1}),1.0]])]});}
            var Q67;
            {var subQ0=sQuery(id+"F0.wireOp",EDGE,"E5");var subQ1=sQuery(id+"F0.wireOp",EDGE,"E2");var subQ2=makeQuery(id+"F0.imprint","INTERSECT",VERTEX,{"derivedFrom":[subQ1,subQ0]});Q67=makeQuery(id+"F0.imprint","IMPRINT",FACE,{"disambiguationData":[TD([[makeQuery(id+"F0.imprint","IMPRINT",EDGE,{"disambiguationData":[TD([[subQ2,1.0]])],"derivedFrom":subQ1}),1.0]])]});}
            var Q68;
            {var subQ0=sQuery(id+"F0.wireOp",EDGE,"E5");var subQ1=sQuery(id+"F0.wireOp",EDGE,"E2");var subQ2=makeQuery(id+"F0.imprint","INTERSECT",VERTEX,{"derivedFrom":[subQ1,subQ0]});Q68=makeQuery(id+"F0.imprint","IMPRINT",FACE,{"disambiguationData":[TD([[makeQuery(id+"F0.imprint","IMPRINT",EDGE,{"disambiguationData":[TD([[subQ2,-1.0]])],"derivedFrom":subQ1}),1.0]])]});}
            var Q69;
            {var subQ2=sQuery(id+"F0.wireOp",EDGE,"E24");var subQ5=sQuery(id+"F0.wireOp",EDGE,"E2");var subQ8=makeQuery(id+"F0.imprint","INTERSECT",VERTEX,{"derivedFrom":[subQ5,subQ2]});Q69=makeQuery(id+"F0.imprint","IMPRINT",FACE,{"disambiguationData":[TD([[makeQuery(id+"F0.imprint","IMPRINT",EDGE,{"disambiguationData":[TD([[subQ8,-1.0]])],"derivedFrom":subQ5}),1.0]])]});}
            var Q70;
            {var subQ4=sQuery(id+"F0.wireOp",EDGE,"E18");var subQ5=sQuery(id+"F0.wireOp",EDGE,"E2");var subQ6=makeQuery(id+"F0.imprint","INTERSECT",VERTEX,{"derivedFrom":[subQ5,subQ4]});Q70=makeQuery(id+"F0.imprint","IMPRINT",FACE,{"disambiguationData":[TD([[makeQuery(id+"F0.imprint","IMPRINT",EDGE,{"disambiguationData":[TD([[subQ6,1.0]])],"derivedFrom":subQ5}),1.0]])]});}
            var Q71;
            {var subQ0=sQuery(id+"F0.wireOp",EDGE,"E25");var subQ1=sQuery(id+"F0.wireOp",EDGE,"E2");var subQ2=makeQuery(id+"F0.imprint","INTERSECT",VERTEX,{"derivedFrom":[subQ1,subQ0]});Q71=makeQuery(id+"F0.imprint","IMPRINT",FACE,{"disambiguationData":[TD([[makeQuery(id+"F0.imprint","IMPRINT",EDGE,{"disambiguationData":[TD([[subQ2,-1.0]])],"derivedFrom":subQ1}),1.0]])]});}
            extrude(context, id + "F3", {"entities" : qUnion([Q0, Q1, Q2, Q3, Q4, Q5, Q6, Q7, Q8, Q9, Q10, Q11, Q12, Q13, Q14, Q15, Q16, Q17, Q18, Q19, Q20, Q21, Q22, Q23, Q24, Q25, Q26, Q27, Q28, Q29, Q30, Q31, Q32, Q33, Q34, Q35, Q36, Q37, Q38, Q39, Q40, Q41, Q42, Q43, Q44, Q45, Q46, Q47, Q48, Q49, Q50, Q51, Q52, Q53, Q54, Q55, Q56, Q57, Q58, Q59, Q60, Q61, Q62, Q63, Q64, Q65, Q66, Q67, Q68, Q69, Q70, Q71]), "operationType" : NewBodyOperationType.ADD, "depth" : 28.2 * mm, "offsetDistance" : 25.4 * mm});
        }
        {
            var Q0;
            {var subQ5=sQuery(id+"F0.wireOp",EDGE,"E3");var subQ13=sQuery(id+"F0.wireOp",EDGE,"E2");var subQ14=makeQuery(id+"F0.imprint","INTERSECT",VERTEX,{"derivedFrom":[subQ13,subQ5]});Q0=makeQuery(id+"F0.imprint","IMPRINT",FACE,{"disambiguationData":[TD([[makeQuery(id+"F0.imprint","IMPRINT",EDGE,{"disambiguationData":[TD([[subQ14,-1.0]])],"derivedFrom":subQ13}),1.0]])]});}
            var Q1;
            {var subQ0=sQuery(id+"F0.wireOp",EDGE,"E8");var subQ1=sQuery(id+"F0.wireOp",EDGE,"E3");var subQ2=makeQuery(id+"F0.imprint","INTERSECT",VERTEX,{"derivedFrom":[subQ1,subQ0]});Q1=makeQuery(id+"F0.imprint","IMPRINT",FACE,{"disambiguationData":[TD([[makeQuery(id+"F0.imprint","IMPRINT",EDGE,{"disambiguationData":[TD([[subQ2,-1.0]])],"derivedFrom":subQ1}),1.0]])]});}
            var Q2;
            {var subQ4=sQuery(id+"F0.wireOp",EDGE,"E4");Q2=makeQuery(id+"F0.imprint","IMPRINT",FACE,{"disambiguationData":[TD([[makeQuery(id+"F0.imprint","IMPRINT",EDGE,{"derivedFrom":subQ4}),-1.0]])]});}
            extrude(context, id + "F4", {"entities" : qUnion([Q0, Q1, Q2]), "operationType" : NewBodyOperationType.ADD, "depth" : 25.66 * mm, "offsetDistance" : 25.4 * mm});
        }
        {
            var Q0;
            Q0=makeQuery(id+"F1.imprint","IMPRINT",FACE,{"disambiguationData":[TD([[makeQuery(id+"F1.imprint","IMPRINT",EDGE,{"derivedFrom":sQuery(id+"F1.wireOp",EDGE,"E116")}),1.0]])]});
            extrude(context, id + "F5", {"entities" : qUnion([Q0]), "depth" : 28.2 * mm, "offsetDistance" : 25.4 * mm, "hasSecondDirection" : true, "secondDirectionOppositeDirection" : false, "secondDirectionDepth" : 25.66 * mm});
        }
    });
